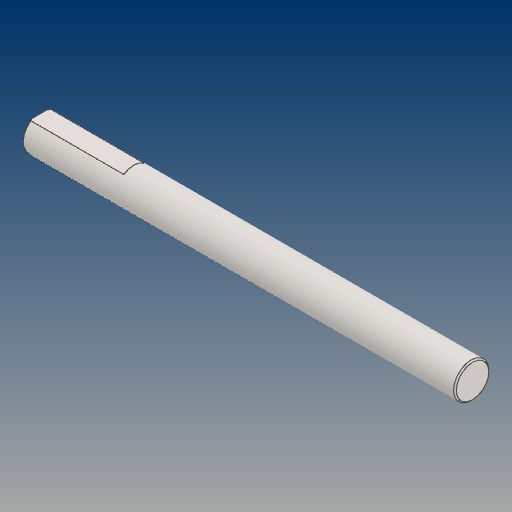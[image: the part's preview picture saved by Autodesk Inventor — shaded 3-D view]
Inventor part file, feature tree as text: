
AUTODESK INVENTOR PART (.ipt)
format: ipt  version: 2021 (Build 250183000, 183)  size: 94,208 bytes
history: native  units: mm
features: chamfer x1
ambient origin geometry x8: Origin, YZ Plane, XZ Plane, XY Plane, X Axis, Y Axis, Z Axis, Center Point
bodies: Solid1 (feature_tree)
feature tree (1):
  chamfer  "Chamfer1"  [1 undecoded]
note: 1 required parameter value undecoded (feature->parameter linkage not recoverable at this tier; creation-order binding heuristic only, values carry confidence <= 0.55)
